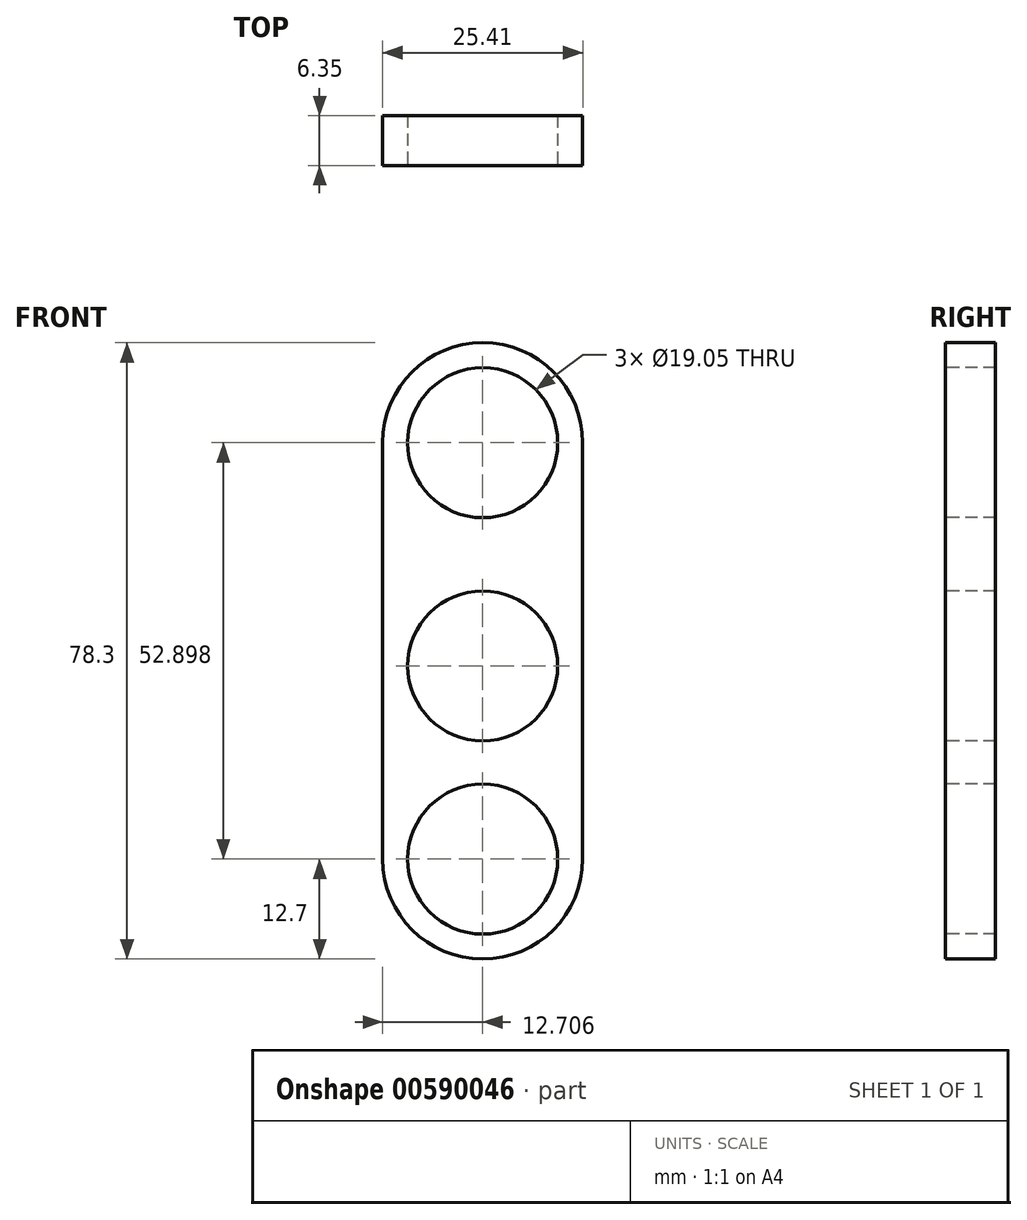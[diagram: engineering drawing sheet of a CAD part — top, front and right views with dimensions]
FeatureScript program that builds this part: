
annotation { "Feature Type Name" : "Feature", "Feature Type Description" : "" }
export const myFeature = defineFeature(function(context is Context, id is Id, definition is map)
    precondition{}
    {
        {
            var Q0;
            Q0=qCreatedBy(makeId("Front.planeOp"),FACE);
            var sketch = newSketch(context, id + "F0", { "sketchPlane" : qUnion([Q0])});
            skLineSegment(sketch, "E0", {"start": v(-63.93, 52.9) * mm, "end": v(-63.93, 0) * mm});
            skLineSegment(sketch, "E1", {"start": v(-38.52, 52.9) * mm, "end": v(-38.52, 0) * mm});
            skArc(sketch, "E2", {"start": v(-38.52, 52.9) * mm, "mid": v(-51.22, 65.6) * mm, "end": v(-63.93, 52.9) * mm});
            skArc(sketch, "E3", {"start": v(-63.93, 0) * mm, "mid": v(-51.22, -12.7) * mm, "end": v(-38.52, 0) * mm});
            skSolve(sketch);
        }
        {
            var Q0;
            Q0=makeQuery(id+"F0.imprint","IMPRINT",FACE,{"disambiguationData":[TD([[makeQuery(id+"F0.imprint","IMPRINT",EDGE,{"derivedFrom":sQuery(id+"F0.wireOp",EDGE,"E0")}),1.0]])]});
            extrude(context, id + "F1", {"entities" : qUnion([Q0]), "depth" : 6.35 * mm, "offsetDistance" : 25.4 * mm});
        }
        {
            var Q0;
            Q0=makeQuery(id+"F1.opExtrude","CAP_FACE",FACE,{"disambiguationData":[OSD([sQuery(id+"F0.wireOp",EDGE,"E0"),sQuery(id+"F0.wireOp",EDGE,"E1"),sQuery(id+"F0.wireOp",EDGE,"E2"),sQuery(id+"F0.wireOp",EDGE,"E3")])],"isStart":false});
            var sketch = newSketch(context, id + "F2", { "sketchPlane" : qUnion([Q0])});
            skCircle(sketch, "E4", {"center": v(-51.22, 52.9) * mm, "radius": 9.53 * mm});
            skCircle(sketch, "E5", {"center": v(-51.22, 24.54) * mm, "radius": 9.53 * mm});
            skCircle(sketch, "E6", {"center": v(-51.22, 0) * mm, "radius": 9.53 * mm});
            skSolve(sketch);
        }
        {
            var Q0;
            Q0=makeQuery(id+"F2.imprint","IMPRINT",FACE,{"disambiguationData":[TD([[makeQuery(id+"F2.imprint","IMPRINT",EDGE,{"derivedFrom":sQuery(id+"F2.wireOp",EDGE,"E5")}),1.0]])]});
            var Q1;
            Q1=makeQuery(id+"F2.imprint","IMPRINT",FACE,{"disambiguationData":[TD([[makeQuery(id+"F2.imprint","IMPRINT",EDGE,{"derivedFrom":sQuery(id+"F2.wireOp",EDGE,"E6")}),1.0]])]});
            var Q2;
            Q2=makeQuery(id+"F2.imprint","IMPRINT",FACE,{"disambiguationData":[TD([[makeQuery(id+"F2.imprint","IMPRINT",EDGE,{"derivedFrom":sQuery(id+"F2.wireOp",EDGE,"E4")}),1.0]])]});
            extrude(context, id + "F3", {"entities" : qUnion([Q0, Q1, Q2]), "operationType" : NewBodyOperationType.REMOVE, "oppositeDirection" : true, "depth" : 25.4 * mm, "offsetDistance" : 25.4 * mm});
        }
    });
